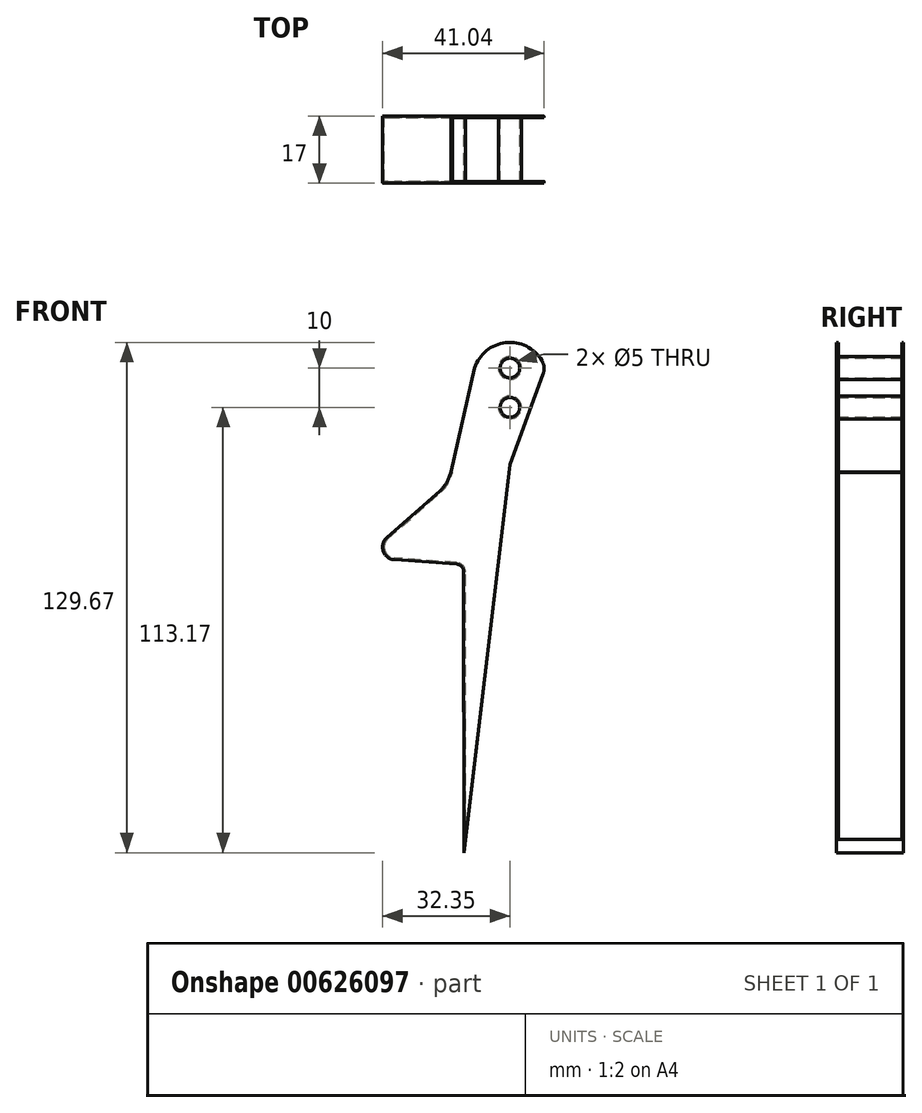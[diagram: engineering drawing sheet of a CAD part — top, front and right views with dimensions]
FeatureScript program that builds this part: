
annotation { "Feature Type Name" : "Feature", "Feature Type Description" : "" }
export const myFeature = defineFeature(function(context is Context, id is Id, definition is map)
    precondition{}
    {
        {
            var Q0;
            Q0=qCreatedBy(makeId("Front.planeOp"),FACE);
            var sketch = newSketch(context, id + "F0", { "sketchPlane" : qUnion([Q0])});
            skCircle(sketch, "E0", {"center": v(0, 0) * mm, "radius": 2.5 * mm});
            skCircle(sketch, "E1", {"center": v(0, -10) * mm, "radius": 2.5 * mm});
            skArc(sketch, "E2", {"start": v(8.1, 1.93) * mm, "mid": v(-1.06, 6.44) * mm, "end": v(-9, 0) * mm});
            skLineSegment(sketch, "E3", {"start": v(8.44, -1.52) * mm, "end": v(0, -24.5) * mm});
            skLineSegment(sketch, "E4", {"start": v(0, -24.5) * mm, "end": v(-12.28, -128.46) * mm});
            skLineSegment(sketch, "E5", {"start": v(-15.23, -120.7) * mm, "end": v(7.68, -141.1) * mm});
            skLineSegment(sketch, "E6", {"start": v(7.68, -141.1) * mm, "end": v(3.26, -141.1) * mm});
            skLineSegment(sketch, "E7", {"start": v(2.18, -140.8) * mm, "end": v(-15.8, -129.3) * mm});
            skLineSegment(sketch, "E8", {"start": v(-11.64, -136.88) * mm, "end": v(-11.73, -51.81) * mm});
            skLineSegment(sketch, "E9", {"start": v(-13.59, -49.82) * mm, "end": v(-29.38, -48.7) * mm});
            skLineSegment(sketch, "E10", {"start": v(-32.35, -45.5) * mm, "end": v(-32.35, -45.47) * mm});
            skLineSegment(sketch, "E11", {"start": v(-31.27, -43.07) * mm, "end": v(-17.81, -31.2) * mm});
            skLineSegment(sketch, "E12", {"start": v(-15, -26.44) * mm, "end": v(-9, 0) * mm});
            skPoint(sketch, "E13.visualSharp", {"position": v(-32.35, -44.02) * mm});
            skArc(sketch, "E13.filletArc", {"start": v(-31.27, -43.07) * mm, "mid": v(-32.07, -44.15) * mm, "end": v(-32.35, -45.47) * mm});
            skPoint(sketch, "E14.visualSharp", {"position": v(-32.35, -48.48) * mm});
            skArc(sketch, "E14.filletArc", {"start": v(-32.35, -45.5) * mm, "mid": v(-31.5, -47.68) * mm, "end": v(-29.38, -48.7) * mm});
            skPoint(sketch, "E15.visualSharp", {"position": v(-11.73, -49.95) * mm});
            skArc(sketch, "E15.filletArc", {"start": v(-11.73, -51.81) * mm, "mid": v(-12.27, -50.45) * mm, "end": v(-13.59, -49.82) * mm});
            skPoint(sketch, "E16.visualSharp", {"position": v(-15.63, -29.27) * mm});
            skArc(sketch, "E16.filletArc", {"start": v(-17.81, -31.2) * mm, "mid": v(-16.03, -29.04) * mm, "end": v(-15, -26.44) * mm});
            skPoint(sketch, "E17.visualSharp", {"position": v(-11.65, -131.95) * mm});
            skArc(sketch, "E17.filletArc", {"start": v(-15.8, -129.3) * mm, "mid": v(-28.53, -141.21) * mm, "end": v(-11.64, -136.88) * mm});
            skPoint(sketch, "E18.visualSharp", {"position": v(2.68, -141.1) * mm});
            skArc(sketch, "E18.filletArc", {"start": v(2.18, -140.8) * mm, "mid": v(2.7, -141.03) * mm, "end": v(3.26, -141.1) * mm});
            skPoint(sketch, "E19.visualSharp", {"position": v(-11.73, -123.8) * mm});
            skArc(sketch, "E19.filletArc", {"start": v(-15.23, -120.7) * mm, "mid": v(-29.64, -130.6) * mm, "end": v(-12.28, -128.46) * mm});
            skPoint(sketch, "E20.visualSharp", {"position": v(9, 0) * mm});
            skArc(sketch, "E20.filletArc", {"start": v(8.44, -1.52) * mm, "mid": v(8.67, 0.24) * mm, "end": v(8.1, 1.93) * mm});
            skSolve(sketch);
        }
        {
            var Q0;
            Q0=makeQuery(id+"F0.imprint","IMPRINT",FACE,{"disambiguationData":[TD([[makeQuery(id+"F0.imprint","IMPRINT",EDGE,{"derivedFrom":sQuery(id+"F0.wireOp",EDGE,"E0")}),-1.0]])]});
            extrude(context, id + "F1", {"entities" : qUnion([Q0]), "depth" : 17 * mm, "offsetDistance" : 25 * mm});
        }
        {
            var Q0;
            Q0=makeQuery(id+"F1.opExtrude","SWEPT_FACE",FACE,{"disambiguationData":[OSD([sQuery(id+"F0.wireOp",EDGE,"E4")])]});
            var Q1;
            Q1=makeQuery(id+"F1.opExtrude","SWEPT_FACE",FACE,{"disambiguationData":[OSD([sQuery(id+"F0.wireOp",EDGE,"E3")])]});
            var Q2;
            Q2=makeQuery(id+"F1.opExtrude","SWEPT_FACE",FACE,{"disambiguationData":[OSD([sQuery(id+"F0.wireOp",EDGE,"E2")])]});
            var Q3;
            Q3=makeQuery(id+"F1.opExtrude","SWEPT_FACE",FACE,{"disambiguationData":[OSD([sQuery(id+"F0.wireOp",EDGE,"E20.filletArc")])]});
            var Q4;
            Q4=makeQuery(id+"F1.opExtrude","SWEPT_FACE",FACE,{"disambiguationData":[OSD([sQuery(id+"F0.wireOp",EDGE,"E12")])]});
            shell(context, id + "F2", {"entities" : qUnion([Q0, Q1, Q2, Q3, Q4]), "thickness" : 0.4 * mm});
        }
    });
